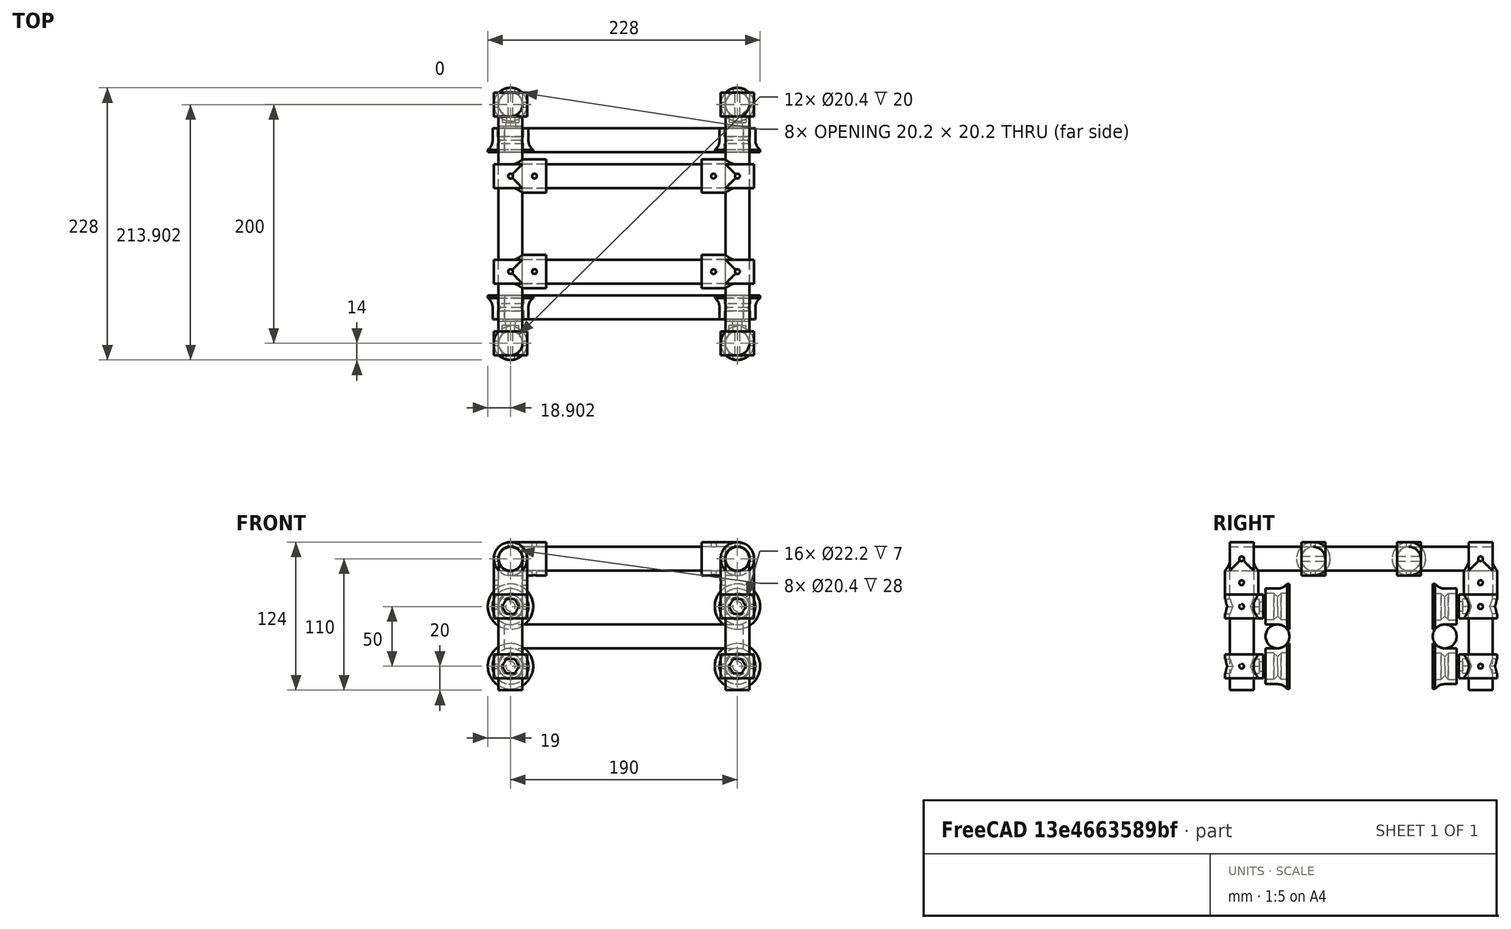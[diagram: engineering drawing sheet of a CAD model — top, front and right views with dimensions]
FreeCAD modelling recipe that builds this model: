
FCSTD DOCUMENT  (FreeCAD 0.17R13522 (Git))
Label: mavis
License: All rights reserved
LicenseURL: http://en.wikipedia.org/wiki/All_rights_reserved
objects: Part::FeaturePython×24, Part::Cylinder×10, App::Part×3
note: 34 computed .brp shape members not serialized (recipe doc carries the construction recipe); baked Part::Feature solids carry a one-line shape summary decoded from their .brp

FEATURE [Part::Cylinder] Cylinder
  Angle = 360
  AttacherType = Attacher::AttachEngine3D
  Height = 200
  Placement = pos=(-100,70,0) rot=(0,1,0;1.5708rad)
  Radius = 10
FEATURE [Part::Cylinder] Cylinder001
  Angle = 360
  AttacherType = Attacher::AttachEngine3D
  Height = 200
  Placement = pos=(-100,-70,0) rot=(0,1,0;1.5708rad)
  Radius = 10
FEATURE [App::Part] Part  label="Rail"
  Group = -> [Cylinder,Cylinder001]
  License = CC BY 3.0
  LicenseURL = http://creativecommons.org/licenses/by/3.0/
  Origin = -> Origin
FEATURE [Part::FeaturePython] wheel_01  # a2plus imported part (geometry in sourceFile) (typed FeaturePython)
  Placement = pos=(-95,-60,25) rot=(1,0,0;1.5708rad)
  fixedPosition = true
  sourceFile = <userpath>/repo/mavis/cad/base/wheel.fcstd
  timeLastImport = 1.54208e+09
  updateColors = true
FEATURE [Part::FeaturePython] wheel_002  # a2plus imported part (geometry in sourceFile) (typed FeaturePython)
  Placement = pos=(-95,60,-25) rot=(-1,0,0;1.5708rad)
  fixedPosition = true
  sourceFile = <userpath>/repo/mavis/cad/base/wheel.fcstd
  timeLastImport = 1.54208e+09
  updateColors = true
FEATURE [Part::FeaturePython] wheel_003  # a2plus imported part (geometry in sourceFile) (typed FeaturePython)
  Placement = pos=(-95,-60,-25) rot=(1,0,0;1.5708rad)
  fixedPosition = true
  sourceFile = <userpath>/repo/mavis/cad/base/wheel.fcstd
  timeLastImport = 1.54208e+09
  updateColors = true
FEATURE [Part::FeaturePython] wheel_004  # a2plus imported part (geometry in sourceFile) (typed FeaturePython)
  Placement = pos=(-95,60,25) rot=(-1,0,0;1.5708rad)
  fixedPosition = true
  sourceFile = <userpath>/repo/mavis/cad/base/wheel.fcstd
  timeLastImport = 1.54208e+09
  updateColors = true
FEATURE [Part::FeaturePython] wheel_005  # a2plus imported part (geometry in sourceFile) (typed FeaturePython)
  Placement = pos=(95,-60,25) rot=(1,0,0;1.5708rad)
  fixedPosition = true
  sourceFile = <userpath>/repo/mavis/cad/base/wheel.fcstd
  timeLastImport = 1.54208e+09
  updateColors = true
FEATURE [Part::FeaturePython] wheel_006  # a2plus imported part (geometry in sourceFile) (typed FeaturePython)
  Placement = pos=(95,60,25) rot=(-1,0,0;1.5708rad)
  fixedPosition = true
  sourceFile = <userpath>/repo/mavis/cad/base/wheel.fcstd
  timeLastImport = 1.54208e+09
  updateColors = true
FEATURE [Part::FeaturePython] wheel_007  # a2plus imported part (geometry in sourceFile) (typed FeaturePython)
  Placement = pos=(95,60,-25) rot=(-1,0,0;1.5708rad)
  fixedPosition = true
  sourceFile = <userpath>/repo/mavis/cad/base/wheel.fcstd
  timeLastImport = 1.54208e+09
  updateColors = true
FEATURE [Part::FeaturePython] wheel_008  # a2plus imported part (geometry in sourceFile) (typed FeaturePython)
  Placement = pos=(95,-60,-25) rot=(1,0,0;1.5708rad)
  fixedPosition = true
  sourceFile = <userpath>/repo/mavis/cad/base/wheel.fcstd
  timeLastImport = 1.54208e+09
  updateColors = true
FEATURE [Part::FeaturePython] connector_m8_01  # a2plus imported part (geometry in sourceFile) (typed FeaturePython)
  Placement = pos=(95,100,25) rot=(0,0,1;3.14159rad)
  fixedPosition = false
  sourceFile = <userpath>/repo/mavis/cad/base/connector-m8.fcstd
  timeLastImport = 1.54209e+09
  updateColors = true
FEATURE [Part::FeaturePython] connector_m8_002  # a2plus imported part (geometry in sourceFile) (typed FeaturePython)
  Placement = pos=(95,-100,-25) rot=(0,0,1;0rad)
  fixedPosition = false
  sourceFile = <userpath>/repo/mavis/cad/base/connector-m8.fcstd
  timeLastImport = 1.54209e+09
  updateColors = true
FEATURE [Part::FeaturePython] connector_m8_003  # a2plus imported part (geometry in sourceFile) (typed FeaturePython)
  Placement = pos=(95,100,-25) rot=(0,0,1;3.14159rad)
  fixedPosition = false
  sourceFile = <userpath>/repo/mavis/cad/base/connector-m8.fcstd
  timeLastImport = 1.54209e+09
  updateColors = true
FEATURE [Part::FeaturePython] connector_m8_004  # a2plus imported part (geometry in sourceFile) (typed FeaturePython)
  Placement = pos=(95,-100,25) rot=(0,0,1;0rad)
  fixedPosition = false
  sourceFile = <userpath>/repo/mavis/cad/base/connector-m8.fcstd
  timeLastImport = 1.54209e+09
  updateColors = true
FEATURE [Part::FeaturePython] connector_m8_005  # a2plus imported part (geometry in sourceFile) (typed FeaturePython)
  Placement = pos=(-95,100,25) rot=(0,0,1;3.14159rad)
  fixedPosition = false
  sourceFile = <userpath>/repo/mavis/cad/base/connector-m8.fcstd
  timeLastImport = 1.54209e+09
  updateColors = true
FEATURE [Part::FeaturePython] connector_m8_006  # a2plus imported part (geometry in sourceFile) (typed FeaturePython)
  Placement = pos=(-95,100,-25) rot=(0,0,1;3.14159rad)
  fixedPosition = false
  sourceFile = <userpath>/repo/mavis/cad/base/connector-m8.fcstd
  timeLastImport = 1.54209e+09
  updateColors = true
FEATURE [Part::FeaturePython] connector_m8_007  # a2plus imported part (geometry in sourceFile) (typed FeaturePython)
  Placement = pos=(-95,-100,25) rot=(0,0,1;0rad)
  fixedPosition = false
  sourceFile = <userpath>/repo/mavis/cad/base/connector-m8.fcstd
  timeLastImport = 1.54209e+09
  updateColors = true
FEATURE [Part::FeaturePython] connector_m8_008  # a2plus imported part (geometry in sourceFile) (typed FeaturePython)
  Placement = pos=(-95,-100,-25) rot=(0,0,1;0rad)
  fixedPosition = false
  sourceFile = <userpath>/repo/mavis/cad/base/connector-m8.fcstd
  timeLastImport = 1.54209e+09
  updateColors = true
FEATURE [App::Part] Part001  label="Wheels And Holders"
  Group = -> [wheel_01,wheel_002,wheel_003,wheel_004,wheel_005,wheel_006,wheel_007,wheel_008,connector_m8_01,connector_m8_002,connector_m8_003,connector_m8_004,connector_m8_005,connector_m8_006,connector_m8_007,connector_m8_008]
  License = CC BY 3.0
  LicenseURL = http://creativecommons.org/licenses/by/3.0/
  Origin = -> Origin001
FEATURE [Part::Cylinder] Cylinder002
  Angle = 360
  AttacherType = Attacher::AttachEngine3D
  Height = 220
  Placement = pos=(-95,-110,65) rot=(-1,0,0;1.5708rad)
  Radius = 10
FEATURE [Part::Cylinder] Cylinder003
  Angle = 360
  AttacherType = Attacher::AttachEngine3D
  Height = 100
  Placement = pos=(95,-100,-45) rot=(0,0,1;0rad)
  Radius = 10
FEATURE [Part::Cylinder] Cylinder004
  Angle = 360
  AttacherType = Attacher::AttachEngine3D
  Height = 100
  Placement = pos=(-95,-100,-45) rot=(0,0,1;0rad)
  Radius = 10
FEATURE [Part::Cylinder] Cylinder005
  Angle = 360
  AttacherType = Attacher::AttachEngine3D
  Height = 100
  Placement = pos=(-95,100,-45) rot=(0,0,1;0rad)
  Radius = 10
FEATURE [Part::FeaturePython] connector_t_01  # a2plus imported part (geometry in sourceFile) (typed FeaturePython)
  Placement = pos=(95,100,65) rot=(0,1,0;1.5708rad)
  fixedPosition = false
  sourceFile = <userpath>/repo/mavis/cad/base/connector-t.fcstd
  timeLastImport = 1.54209e+09
  updateColors = true
FEATURE [Part::FeaturePython] connector_t_002  # a2plus imported part (geometry in sourceFile) (typed FeaturePython)
  Placement = pos=(-95,100,65) rot=(0,1,0;1.5708rad)
  fixedPosition = false
  sourceFile = <userpath>/repo/mavis/cad/base/connector-t.fcstd
  timeLastImport = 1.54209e+09
  updateColors = true
FEATURE [Part::FeaturePython] connector_t_003  # a2plus imported part (geometry in sourceFile) (typed FeaturePython)
  Placement = pos=(95,40,65) rot=(0,1,0;3.14159rad)
  fixedPosition = false
  sourceFile = <userpath>/repo/mavis/cad/base/connector-t.fcstd
  timeLastImport = 1.54209e+09
  updateColors = true
FEATURE [Part::FeaturePython] connector_t_004  # a2plus imported part (geometry in sourceFile) (typed FeaturePython)
  Placement = pos=(95,-100,65) rot=(0,1,0;1.5708rad)
  fixedPosition = false
  sourceFile = <userpath>/repo/mavis/cad/base/connector-t.fcstd
  timeLastImport = 1.54209e+09
  updateColors = true
FEATURE [Part::Cylinder] Cylinder006
  Angle = 360
  AttacherType = Attacher::AttachEngine3D
  Height = 100
  Placement = pos=(95,100,-45) rot=(0,0,1;0rad)
  Radius = 10
FEATURE [Part::Cylinder] Cylinder007
  Angle = 360
  AttacherType = Attacher::AttachEngine3D
  Height = 170
  Placement = pos=(85,40,65) rot=(0.57735,0.57735,-0.57735;4.18879rad)
  Radius = 10
FEATURE [Part::FeaturePython] connector_t_005  # a2plus imported part (geometry in sourceFile) (typed FeaturePython)
  Placement = pos=(-95,-100,65) rot=(0,1,0;1.5708rad)
  fixedPosition = false
  sourceFile = <userpath>/repo/mavis/cad/base/connector-t.fcstd
  timeLastImport = 1.54209e+09
  updateColors = true
FEATURE [Part::FeaturePython] connector_t_006  # a2plus imported part (geometry in sourceFile) (typed FeaturePython)
  Placement = pos=(95,-40,65) rot=(0,1,0;3.14159rad)
  fixedPosition = false
  sourceFile = <userpath>/repo/mavis/cad/base/connector-t.fcstd
  timeLastImport = 1.54209e+09
  updateColors = true
FEATURE [Part::FeaturePython] connector_t_007  # a2plus imported part (geometry in sourceFile) (typed FeaturePython)
  Placement = pos=(-95,40,65) rot=(0,0,1;0rad)
  fixedPosition = false
  sourceFile = <userpath>/repo/mavis/cad/base/connector-t.fcstd
  timeLastImport = 1.54209e+09
  updateColors = true
FEATURE [Part::Cylinder] Cylinder008
  Angle = 360
  AttacherType = Attacher::AttachEngine3D
  Height = 220
  Placement = pos=(95,-110,65) rot=(-1,0,0;1.5708rad)
  Radius = 10
FEATURE [Part::FeaturePython] connector_t_009  # a2plus imported part (geometry in sourceFile) (typed FeaturePython)
  Placement = pos=(-95,-40,65) rot=(0,0,1;0rad)
  fixedPosition = false
  sourceFile = <userpath>/repo/mavis/cad/base/connector-t.fcstd
  timeLastImport = 1.54209e+09
  updateColors = true
FEATURE [Part::Cylinder] Cylinder009
  Angle = 360
  AttacherType = Attacher::AttachEngine3D
  Height = 170
  Placement = pos=(85,-40,65) rot=(0.57735,0.57735,-0.57735;4.18879rad)
  Radius = 10
FEATURE [App::Part] Part002  label="Base"
  Group = -> [Cylinder002,Cylinder003,Cylinder004,Cylinder005,connector_t_01,connector_t_002,connector_t_003,connector_t_004,Cylinder006,Cylinder007,connector_t_005,connector_t_006,connector_t_007,Cylinder008,connector_t_009,Cylinder009]
  License = CC BY 3.0
  LicenseURL = http://creativecommons.org/licenses/by/3.0/
  Origin = -> Origin002
